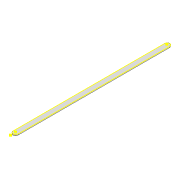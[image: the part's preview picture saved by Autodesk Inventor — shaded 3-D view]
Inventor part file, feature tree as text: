
AUTODESK INVENTOR PART (.ipt)
format: ipt  version: 2022 (Build 260153000, 153)  size: 107,008 bytes
history: native  units: mm
features: extrude x3, sketch x3, projected_geometry x2
ambient origin geometry x8: Origin, YZ Plane, XZ Plane, XY Plane, X Axis, Y Axis, Z Axis, Center Point
bodies: Solid1 (feature_tree)
feature tree (8):
  extrude  "Extrusion1"  Depth=8.0mm
  sketch  "Sketch2"  dims[d2=3.0mm d3=3.0mm]
  extrude  "Extrusion2"  Depth=3.0mm
  extrude  "Extrusion3"  Depth=8.0mm
  sketch  "Sketch3"  dims[d4=4.5mm d5=0.0mm d6=8.0mm d7=16.0mm d8=8.0mm d9=2.0mm d10=0.0mm d11=100.0mm d12=0.0mm]
  sketch  "Sketch1"  dims[d0=263.803mm d1=8.0mm]
  projected_geometry  "Projected Loop1"
  projected_geometry  "Projected Loop2"
